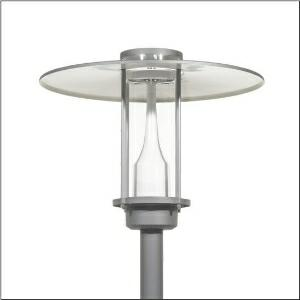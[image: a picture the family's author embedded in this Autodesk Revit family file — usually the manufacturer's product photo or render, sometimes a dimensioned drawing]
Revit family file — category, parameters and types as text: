
# Revit family: city-light_plus_iq___st1_2a_5xa5275ef14hp_0b83
name_source: partatom
category: Lighting Fixtures
units: mm (PartAtom-declared; Revit-internal decimal feet)

## family parameters
Cut with Voids When Loaded = No
Host = Face
Light Source = No
Part Type = Normal
Room Calculation Point = No
Round Connector Dimension = Use Diameter
Shared = No

## types (1)
- --- (1 x LED, 4510 lm, 33.6 W, 3000K)
    Apparent Load = 34 VA
    CIE Flux Codes = 22 60 93 97 100
    Color Rendering = 70
    Color Temperature = 3000K
    Default Elevation = 1800 mm
    Description = City-Light Plus iQ, mast luminaire, Module 540 iQ-SR, primary light control with 3 zone facetted reflector, of plastic, silver coated, highly specular, structured, primary optical cover: cover, of PMMA, transparent, light distribution: ST1.2a, light emission: direct distribution, primary light characteristic: asymmetric, installation type: post-top, LED, High Power LED, rated luminous flux: 4.510lm, luminous efficacy: 134lm/W, light colour: 730, colour temperature: 3000K, control gear: ECG iQ, control: presetting dimming logarithmic, Street-Remote, Auto-Match, Temp-Guard, Lumen-Switch, Night-Set, Smart-Wire, Light-Fading, Desk-Remote (wireless, voltage-free reading and setting of iQ features in the workshop via application-optimized NFC function/RFID function), optimised constant luminous flux control (CLO 2.0), with terminal, 6-pole, max. 2.5mm², mains connection: 220..240V, AC, 50/60Hz, start of lifetime: 34W, end of lifetime: 36W, reduction: 15W, luminaire housing, upper part, of glass-fibre reinforced polyester, coated, Siteco® metallic grey (DB 702S), diameter: 750mm, height: 590mm, spigot size: d x l = 76 x 70mm (post-top) | with reducer (optional accessory) 60 x 70mm, post-top mast mounting element, of diecast aluminium, coated, Siteco® metallic grey (DB 702S), Module 540 iQ-SR, traffic white (RAL 9016), equipment: Power, protection rating (complete): IP65, insulation class (complete): insulation class II (safety insulation), certification: CE, ENEC, VDE, packaging unit: 1 piece

Light Distribution: ST1.2a
    Height = 590 mm
    Lamp = 1 x LED
    Lamp Light Flux = 4510 lm
    Lamp Power = 33.6 W
    Lamp count = 1
    Length = 750 mm
    Luminous efficacy = 134 lm/W
    Manufacturer = Siteco
    ModVariant = No
    Model = 5XA5275EF14HP
    Number of Poles = 1
    OnlyDefault = Yes
    Power Factor = 1
    Product Name = City-Light Plus iQ | ST1.2a
    Product group = mast luminaire | pylon top
    ProductGroupID = 6100
    Protection Class = Protection class II
    Protection Degree = IP 65
    RLX_Detail_Level = 1
    RlxData = <blob elided: 52549 chars, md5=7ac61983>
    Socket = socket
    Standby Power = 0 W
    System Light Flux = 4510 lm
    System Power = 34 W
    Type Comments = factory setting: luminous flux: 100 % | dim-lin: 254 | 695 mA
    Type Image = l_1006456.jpg
    URL = http://relux.com
    VarID = @adj_114533
    Voltage = 0 V
    Weight = 0.00 kg
    Width = 0 mm  [stored 0 ft]

note: [stored X ft] marks values corroborated as IEEE doubles in the binary element streams (Revit-internal decimal feet)

## geometry (parser evidence)
native form markers: Blend x4, Sweep x13
no freeform markers — native parametric forms only
